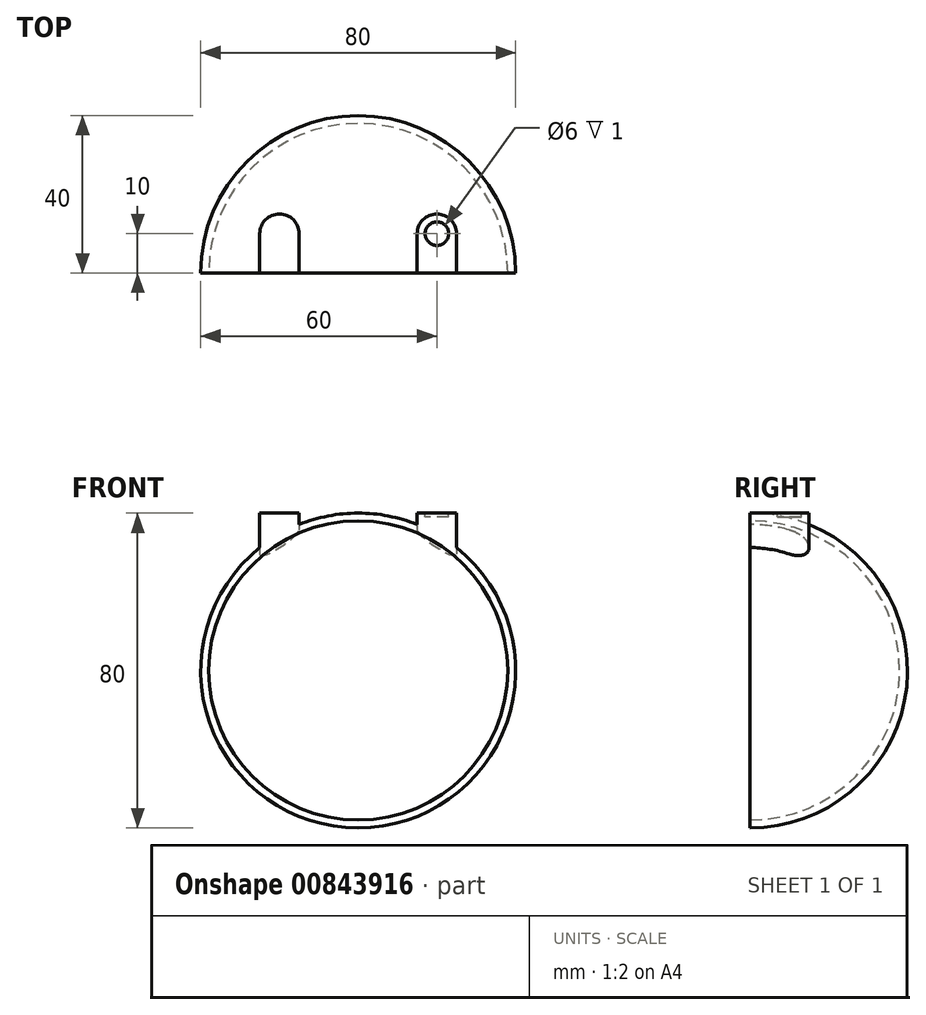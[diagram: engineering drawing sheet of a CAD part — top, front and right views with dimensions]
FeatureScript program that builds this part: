
annotation { "Feature Type Name" : "Feature", "Feature Type Description" : "" }
export const myFeature = defineFeature(function(context is Context, id is Id, definition is map)
    precondition{}
    {
        {
            var Q0;
            Q0=qCreatedBy(makeId("Front.planeOp"),FACE);
            var sketch = newSketch(context, id + "F0", { "sketchPlane" : qUnion([Q0])});
            skArc(sketch, "E0", {"start": v(0, -40) * mm, "mid": v(40, 0) * mm, "end": v(0, 40) * mm});
            skLineSegment(sketch, "E1", {"start": v(0, 0) * mm, "end": v(0, 40) * mm});
            skLineSegment(sketch, "E2", {"start": v(0, 0) * mm, "end": v(0, -40) * mm});
            skSolve(sketch);
        }
        {
            var Q0;
            Q0 = qSketchRegion(id + "F0", true);
            var Q1;
            Q1=sQuery(id+"F0.wireOp",EDGE,"E1");
            revolve(context, id + "F1", {"surfaceOperationType" : NewSurfaceOperationType.NEW, "entities" : qUnion([Q0]), "axis" : qUnion([Q1]), "revolveType" : RevolveType.ONE_DIRECTION, "angle" : 180 * degree});
        }
        {
            var Q0;
            Q0=qCreatedBy(makeId("Top.planeOp"),FACE);
            var sketch = newSketch(context, id + "F2", { "sketchPlane" : qUnion([Q0])});
            skLineSegment(sketch, "E3.bottom", {"start": v(-15, 0) * mm, "end": v(-25, 0) * mm});
            skLineSegment(sketch, "E3.left", {"start": v(-15, 0) * mm, "end": v(-15, 10) * mm});
            skLineSegment(sketch, "E3.right", {"start": v(-25, 0) * mm, "end": v(-25, 10) * mm});
            skPoint(sketch, "E4.oppositeSnap0", {"position": v(-20, 10) * mm});
            skLineSegment(sketch, "E4.bottom", {"start": v(15, 0) * mm, "end": v(25, 0) * mm});
            skLineSegment(sketch, "E4.left", {"start": v(15, 0) * mm, "end": v(15, 10) * mm});
            skLineSegment(sketch, "E4.right", {"start": v(25, 0) * mm, "end": v(25, 10) * mm});
            skLineSegment(sketch, "E5", {"start": v(-20, 10) * mm, "end": v(-20, 0) * mm, "construction": true});
            skLineSegment(sketch, "E6", {"start": v(20, 10) * mm, "end": v(20, 0) * mm, "construction": true});
            skArc(sketch, "E7", {"start": v(-15, 10) * mm, "mid": v(-20, 15) * mm, "end": v(-25, 10) * mm});
            skArc(sketch, "E8", {"start": v(25, 10) * mm, "mid": v(20, 15) * mm, "end": v(15, 10) * mm});
            skSolve(sketch);
        }
        {
            var Q0;
            Q0 = qSketchRegion(id + "F2", true);
            extrude(context, id + "F3", {"entities" : qUnion([Q0]), "operationType" : NewBodyOperationType.ADD, "depth" : 40 * mm, "offsetDistance" : 25 * mm});
        }
        {
            var Q0;
            Q0=makeQuery(id+"F3.boolean.opBoolean","MERGE",FACE,{"derivedFrom":[makeQuery(id+"F1.opRevolve","CAP_FACE",FACE,{"disambiguationData":[OSD([sQuery(id+"F0.wireOp",EDGE,"E0"),sQuery(id+"F0.wireOp",EDGE,"E1"),sQuery(id+"F0.wireOp",EDGE,"E2")])],"isStart":true}),makeQuery(id+"F3.opExtrude","SWEPT_FACE",FACE,{"disambiguationData":[OSD([sQuery(id+"F2.wireOp",EDGE,"E3.bottom")])]}),makeQuery(id+"F3.opExtrude","SWEPT_FACE",FACE,{"disambiguationData":[OSD([sQuery(id+"F2.wireOp",EDGE,"E4.bottom")])]})]});
            var sketch = newSketch(context, id + "F4", { "sketchPlane" : qUnion([Q0])});
            skArc(sketch, "E9", {"start": v(0, -38) * mm, "mid": v(38, 0) * mm, "end": v(0, 38) * mm});
            skLineSegment(sketch, "E10", {"start": v(0, -38) * mm, "end": v(0, 38) * mm});
            skSolve(sketch);
        }
        {
            var Q0;
            Q0 = qSketchRegion(id + "F4", true);
            var Q1;
            Q1=sQuery(id+"F4.wireOp",EDGE,"E10");
            revolve(context, id + "F5", {"operationType" : NewBodyOperationType.REMOVE, "surfaceOperationType" : NewSurfaceOperationType.NEW, "entities" : qUnion([Q0]), "axis" : qUnion([Q1]), "revolveType" : RevolveType.FULL, "oppositeDirection" : true});
        }
        {
            var Q0;
            Q0=makeQuery(id+"F3.opExtrude","CAP_FACE",FACE,{"disambiguationData":[OSD([sQuery(id+"F2.wireOp",EDGE,"E4.bottom"),sQuery(id+"F2.wireOp",EDGE,"E4.left"),sQuery(id+"F2.wireOp",EDGE,"E4.right"),sQuery(id+"F2.wireOp",EDGE,"E8")])],"isStart":false});
            var sketch = newSketch(context, id + "F6", { "sketchPlane" : qUnion([Q0])});
            skCircle(sketch, "E11", {"center": v(20, 10) * mm, "radius": 3 * mm});
            skSolve(sketch);
        }
        {
            var Q0;
            Q0 = qSketchRegion(id + "F6", true);
            extrude(context, id + "F7", {"entities" : qUnion([Q0]), "operationType" : NewBodyOperationType.REMOVE, "oppositeDirection" : true, "depth" : 1 * mm, "offsetDistance" : 25 * mm});
        }
    });
